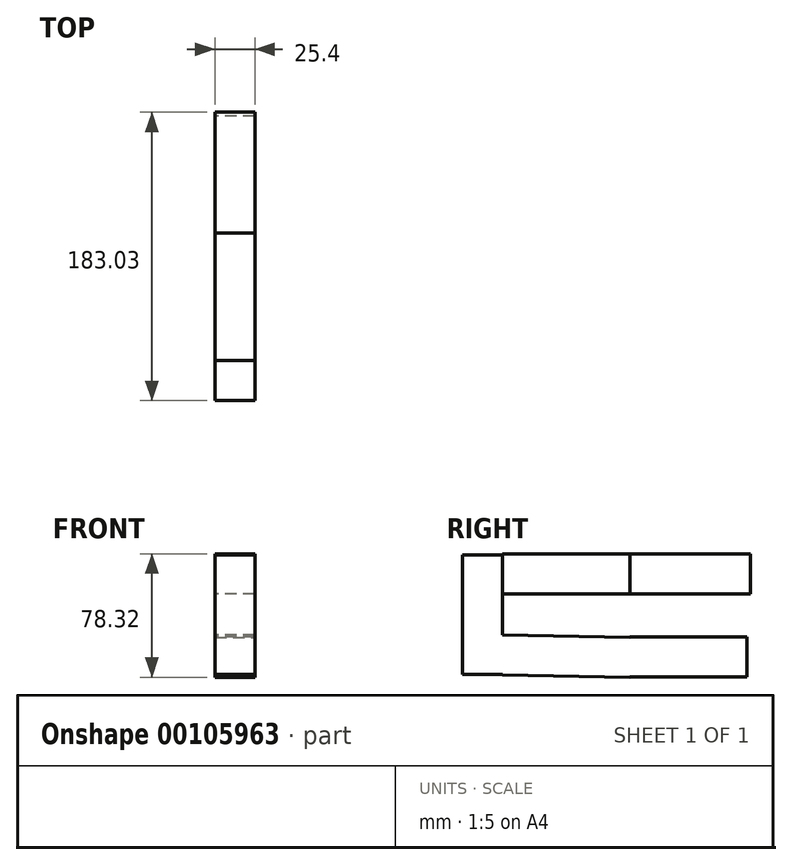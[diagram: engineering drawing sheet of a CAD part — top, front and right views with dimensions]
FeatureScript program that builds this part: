
annotation { "Feature Type Name" : "Feature", "Feature Type Description" : "" }
export const myFeature = defineFeature(function(context is Context, id is Id, definition is map)
    precondition{}
    {
        {
            var Q0;
            Q0=qCreatedBy(makeId("Front.planeOp"),FACE);
            var sketch = newSketch(context, id + "F0", { "sketchPlane" : qUnion([Q0])});
            skArc(sketch, "E0", {"start": v(0, 50.43) * mm, "mid": v(-39.8, 12.14) * mm, "end": v(0, -26.15) * mm});
            skSolve(sketch);
        }
        {
            var Q0;
            Q0=qCreatedBy(makeId("Right.planeOp"),FACE);
            var sketch = newSketch(context, id + "F1", { "sketchPlane" : qUnion([Q0])});
            skLineSegment(sketch, "E1", {"start": v(0, 50.61) * mm, "end": v(81.03, 50.61) * mm});
            skLineSegment(sketch, "E2", {"start": v(0, -26.1) * mm, "end": v(81.03, -27.59) * mm});
            skSolve(sketch);
        }
        {
            var Q0;
            Q0=qCreatedBy(makeId("Right.planeOp"),FACE);
            var sketch = newSketch(context, id + "F2", { "sketchPlane" : qUnion([Q0])});
            skLineSegment(sketch, "E3", {"start": v(80.9, -27.47) * mm, "end": v(155.22, -27.47) * mm});
            skLineSegment(sketch, "E4", {"start": v(81.1, 50.73) * mm, "end": v(157.63, 50.73) * mm});
            skSolve(sketch);
        }
        {
            var Q0;
            Q0=qCreatedBy(makeId("Front.planeOp"),FACE);
            var sketch = newSketch(context, id + "F3", { "sketchPlane" : qUnion([Q0])});
            skLineSegment(sketch, "E5", {"start": v(0, 50.24) * mm, "end": v(0, -25.76) * mm});
            skSolve(sketch);
        }
        {
            var Q0;
            Q0=sQuery(id+"F1.wireOp",EDGE,"E2");
            var Q1;
            Q1=sQuery(id+"F1.wireOp",EDGE,"E1");
            var Q2;
            Q2=sQuery(id+"F2.wireOp",EDGE,"E3");
            var Q3;
            Q3=sQuery(id+"F2.wireOp",EDGE,"E4");
            extrude(context, id + "F4", {"bodyType" : ToolBodyType.SURFACE, "surfaceEntities" : qUnion([Q0, Q1, Q2, Q3]), "oppositeDirection" : true, "depth" : 25.4 * mm});
        }
        {
            var Q0;
            Q0=sQuery(id+"F0.wireOp",EDGE,"E0");
            var Q1;
            Q1=sQuery(id+"F3.wireOp",EDGE,"E5");
            extrude(context, id + "F5", {"bodyType" : ToolBodyType.SURFACE, "surfaceEntities" : qUnion([Q0, Q1]), "depth" : 25.4 * mm});
        }
        {
            var Q0;
            Q0=makeQuery(id+"F5.opExtrude","SWEPT_FACE",FACE,{"disambiguationData":[OSD([sQuery(id+"F3.wireOp",EDGE,"E5")])]});
            extrude(context, id + "F6", {"entities" : qUnion([Q0]), "depth" : 25.4 * mm});
        }
        {
            var Q0;
            Q0=makeQuery(id+"F4.opExtrude","SWEPT_FACE",FACE,{"disambiguationData":[OSD([sQuery(id+"F2.wireOp",EDGE,"E3")])]});
            var Q1;
            Q1=makeQuery(id+"F4.opExtrude","SWEPT_FACE",FACE,{"disambiguationData":[OSD([sQuery(id+"F1.wireOp",EDGE,"E2")])]});
            extrude(context, id + "F7", {"entities" : qUnion([Q0, Q1]), "operationType" : NewBodyOperationType.ADD, "depth" : 25.4 * mm});
        }
        {
            var Q0;
            Q0=makeQuery(id+"F4.opExtrude","SWEPT_FACE",FACE,{"disambiguationData":[OSD([sQuery(id+"F1.wireOp",EDGE,"E1")])]});
            var Q1;
            Q1=makeQuery(id+"F4.opExtrude","SWEPT_FACE",FACE,{"disambiguationData":[OSD([sQuery(id+"F2.wireOp",EDGE,"E4")])]});
            extrude(context, id + "F8", {"entities" : qUnion([Q0, Q1]), "oppositeDirection" : true, "depth" : 25.4 * mm});
        }
    });
